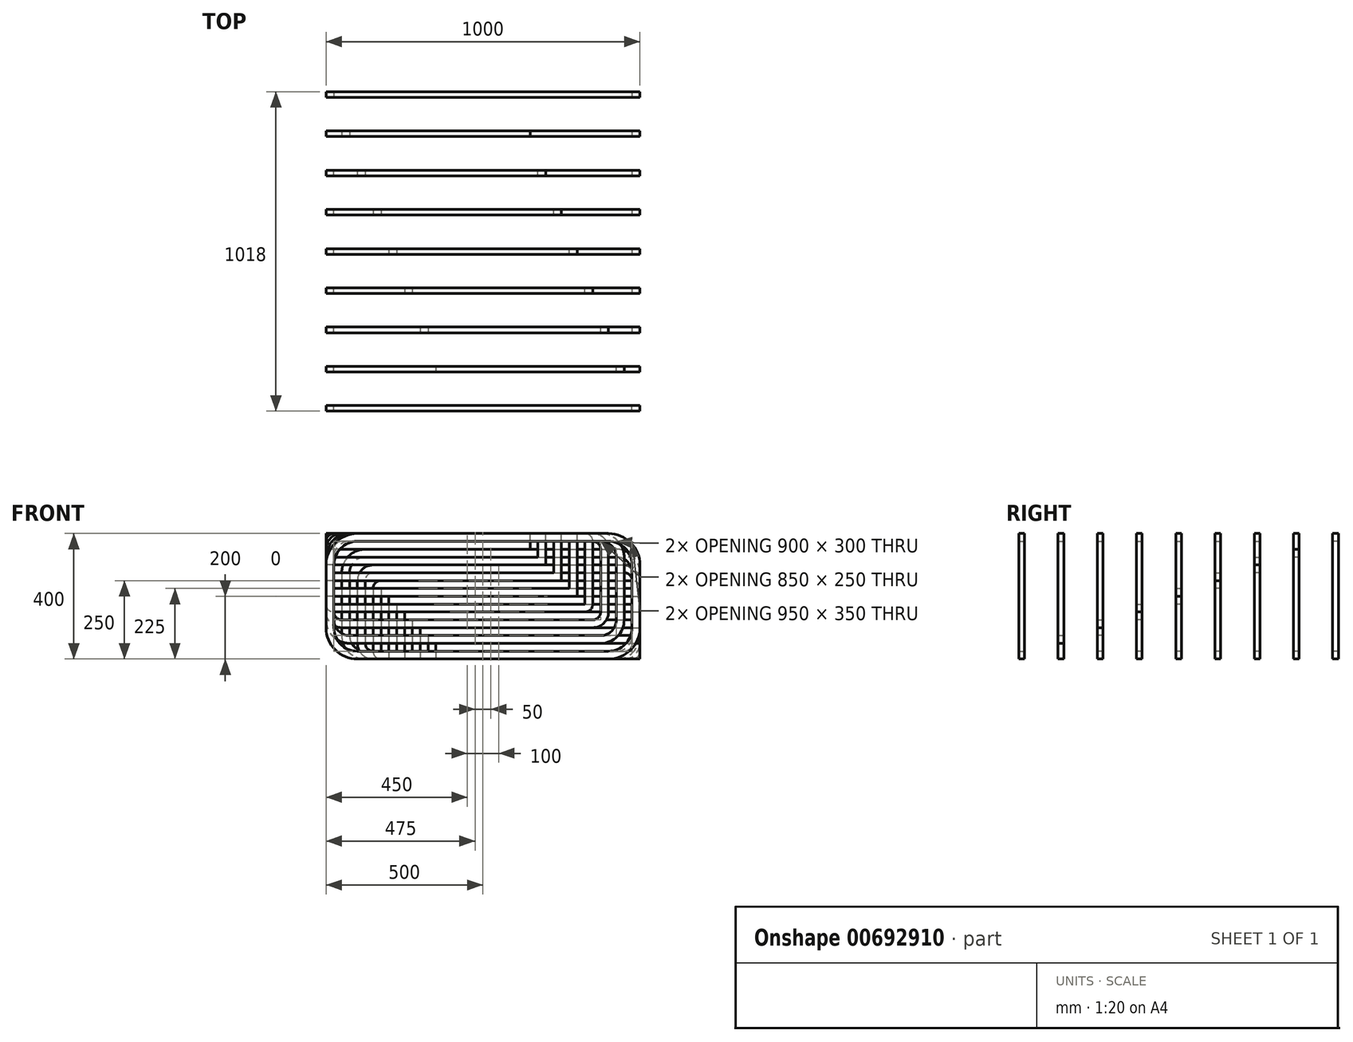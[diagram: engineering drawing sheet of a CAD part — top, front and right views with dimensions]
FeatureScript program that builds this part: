
annotation { "Feature Type Name" : "Feature", "Feature Type Description" : "" }
export const myFeature = defineFeature(function(context is Context, id is Id, definition is map)
    precondition{}
    {
        {
            assignVariable(context, id + "F0", {"name" : "thickness", "anyValue" : 18});
        }
        {
            assignVariable(context, id + "F1", {"name" : "length", "anyValue" : 1000});
        }
        {
            assignVariable(context, id + "F2", {"name" : "width", "anyValue" : getVariable(context, 'length')});
        }
        {
            assignVariable(context, id + "F3", {"name" : "stripwidth", "anyValue" : 25});
        }
        {
            assignVariable(context, id + "F4", {"name" : "interspace", "anyValue" : 5 * getVariable(context, 'stripwidth')});
        }
        {
            var Q0;
            Q0=qCreatedBy(makeId("Front.planeOp"),FACE);
            var sketch = newSketch(context, id + "F5", { "sketchPlane" : qUnion([Q0])});
            skLineSegment(sketch, "E0.bottom", {"start": v(-100, 0) * mm, "end": v(-900, 0) * mm});
            skLineSegment(sketch, "E0.top", {"start": v(-100, 400) * mm, "end": v(-900, 400) * mm});
            skLineSegment(sketch, "E0.left", {"start": v(0, 100) * mm, "end": v(0, 300) * mm});
            skLineSegment(sketch, "E0.right", {"start": v(-1000, 100) * mm, "end": v(-1000, 300) * mm});
            skPoint(sketch, "E1.visualSharp", {"position": v(-1000, 400) * mm});
            skArc(sketch, "E1.filletArc", {"start": v(-900, 400) * mm, "mid": v(-970.71, 370.71) * mm, "end": v(-1000, 300) * mm});
            skPoint(sketch, "E2.visualSharp", {"position": v(0, 400) * mm});
            skArc(sketch, "E2.filletArc", {"start": v(0, 300) * mm, "mid": v(-29.29, 370.71) * mm, "end": v(-100, 400) * mm});
            skPoint(sketch, "E3.visualSharp", {"position": v(0, 0) * mm});
            skArc(sketch, "E3.filletArc", {"start": v(-100, 0) * mm, "mid": v(-29.29, 29.29) * mm, "end": v(0, 100) * mm});
            skPoint(sketch, "E4.visualSharp", {"position": v(-1000, 0) * mm});
            skArc(sketch, "E4.filletArc", {"start": v(-1000, 100) * mm, "mid": v(-970.71, 29.29) * mm, "end": v(-900, 0) * mm});
            skLineSegment(sketch, "E5.0", {"start": v(-975, 100) * mm, "end": v(-975, 300) * mm});
            skArc(sketch, "E5.1", {"start": v(-900, 375) * mm, "mid": v(-953.03, 353.03) * mm, "end": v(-975, 300) * mm});
            skArc(sketch, "E5.2", {"start": v(-975, 100) * mm, "mid": v(-953.03, 46.97) * mm, "end": v(-900, 25) * mm});
            skLineSegment(sketch, "E5.3", {"start": v(-100, 375) * mm, "end": v(-900, 375) * mm});
            skLineSegment(sketch, "E5.4", {"start": v(-100, 25) * mm, "end": v(-900, 25) * mm});
            skArc(sketch, "E5.5", {"start": v(-100, 25) * mm, "mid": v(-46.97, 46.97) * mm, "end": v(-25, 100) * mm});
            skLineSegment(sketch, "E5.6", {"start": v(-25, 100) * mm, "end": v(-25, 300) * mm});
            skArc(sketch, "E5.7", {"start": v(-25, 300) * mm, "mid": v(-46.97, 353.03) * mm, "end": v(-100, 375) * mm});
            skArc(sketch, "E6.0", {"start": v(-50, 300) * mm, "mid": v(-64.64, 335.36) * mm, "end": v(-100, 350) * mm});
            skLineSegment(sketch, "E6.1", {"start": v(-50, 100) * mm, "end": v(-50, 300) * mm});
            skLineSegment(sketch, "E6.2", {"start": v(-100, 350) * mm, "end": v(-900, 350) * mm});
            skArc(sketch, "E6.3", {"start": v(-100, 50) * mm, "mid": v(-64.64, 64.64) * mm, "end": v(-50, 100) * mm});
            skArc(sketch, "E6.4", {"start": v(-900, 350) * mm, "mid": v(-935.36, 335.36) * mm, "end": v(-950, 300) * mm});
            skLineSegment(sketch, "E6.5", {"start": v(-950, 100) * mm, "end": v(-950, 300) * mm});
            skArc(sketch, "E6.6", {"start": v(-950, 100) * mm, "mid": v(-935.36, 64.64) * mm, "end": v(-900, 50) * mm});
            skLineSegment(sketch, "E6.7", {"start": v(-100, 50) * mm, "end": v(-900, 50) * mm});
            skLineSegment(sketch, "E7.0", {"start": v(-100, 325) * mm, "end": v(-900, 325) * mm});
            skArc(sketch, "E7.1", {"start": v(-75, 300) * mm, "mid": v(-82.32, 317.68) * mm, "end": v(-100, 325) * mm});
            skArc(sketch, "E7.2", {"start": v(-900, 325) * mm, "mid": v(-917.68, 317.68) * mm, "end": v(-925, 300) * mm});
            skLineSegment(sketch, "E7.3", {"start": v(-75, 100) * mm, "end": v(-75, 300) * mm});
            skLineSegment(sketch, "E7.4", {"start": v(-925, 100) * mm, "end": v(-925, 300) * mm});
            skArc(sketch, "E7.5", {"start": v(-925, 100) * mm, "mid": v(-917.68, 82.32) * mm, "end": v(-900, 75) * mm});
            skLineSegment(sketch, "E7.6", {"start": v(-100, 75) * mm, "end": v(-900, 75) * mm});
            skArc(sketch, "E7.7", {"start": v(-100, 75) * mm, "mid": v(-82.32, 82.32) * mm, "end": v(-75, 100) * mm});
            skLineSegment(sketch, "E8.0", {"start": v(-100, 300) * mm, "end": v(-900, 300) * mm});
            skLineSegment(sketch, "E8.1", {"start": v(-100, 300) * mm, "end": v(-100, 300) * mm});
            skLineSegment(sketch, "E8.2", {"start": v(-900, 300) * mm, "end": v(-900, 300) * mm});
            skLineSegment(sketch, "E8.3", {"start": v(-100, 100) * mm, "end": v(-100, 300) * mm});
            skLineSegment(sketch, "E8.4", {"start": v(-900, 100) * mm, "end": v(-900, 300) * mm});
            skLineSegment(sketch, "E8.5", {"start": v(-900, 100) * mm, "end": v(-900, 100) * mm});
            skLineSegment(sketch, "E8.6", {"start": v(-100, 100) * mm, "end": v(-900, 100) * mm});
            skLineSegment(sketch, "E8.7", {"start": v(-100, 100) * mm, "end": v(-100, 100) * mm});
            skLineSegment(sketch, "E9.0", {"start": v(-875, 125) * mm, "end": v(-875, 275) * mm});
            skLineSegment(sketch, "E9.1", {"start": v(-125, 125) * mm, "end": v(-875, 125) * mm});
            skLineSegment(sketch, "E9.2", {"start": v(-125, 125) * mm, "end": v(-125, 275) * mm});
            skLineSegment(sketch, "E9.3", {"start": v(-125, 275) * mm, "end": v(-875, 275) * mm});
            skLineSegment(sketch, "E10.0", {"start": v(-850, 150) * mm, "end": v(-850, 250) * mm});
            skLineSegment(sketch, "E10.1", {"start": v(-150, 150) * mm, "end": v(-850, 150) * mm});
            skLineSegment(sketch, "E10.2", {"start": v(-150, 150) * mm, "end": v(-150, 250) * mm});
            skLineSegment(sketch, "E10.3", {"start": v(-150, 250) * mm, "end": v(-850, 250) * mm});
            skLineSegment(sketch, "E11.0", {"start": v(-825, 175) * mm, "end": v(-825, 225) * mm});
            skLineSegment(sketch, "E11.1", {"start": v(-175, 175) * mm, "end": v(-825, 175) * mm});
            skLineSegment(sketch, "E11.2", {"start": v(-175, 175) * mm, "end": v(-175, 225) * mm});
            skLineSegment(sketch, "E11.3", {"start": v(-175, 225) * mm, "end": v(-825, 225) * mm});
            skSolve(sketch);
        }
        {
            var Q0;
            Q0=makeQuery(id+"F5.imprint","IMPRINT",FACE,{"disambiguationData":[TD([[makeQuery(id+"F5.imprint","IMPRINT",EDGE,{"derivedFrom":sQuery(id+"F5.wireOp",EDGE,"E0.bottom")}),-1.0]])]});
            extrude(context, id + "F6", {"entities" : qUnion([Q0]), "depth" : (getVariable(context, 'thickness')) * mm, "offsetDistance" : 25 * mm});
        }
        {
            var Q0;
            Q0=makeQuery(id+"F5.imprint","IMPRINT",FACE,{"disambiguationData":[TD([[makeQuery(id+"F5.imprint","IMPRINT",EDGE,{"derivedFrom":sQuery(id+"F5.wireOp",EDGE,"E5.0")}),-1.0]])]});
            extrude(context, id + "F7", {"entities" : qUnion([Q0]), "depth" : (getVariable(context, 'thickness')) * mm, "offsetDistance" : 25 * mm});
        }
        {
            var Q0;
            Q0=makeQuery(id+"F5.imprint","IMPRINT",FACE,{"disambiguationData":[TD([[makeQuery(id+"F5.imprint","IMPRINT",EDGE,{"derivedFrom":sQuery(id+"F5.wireOp",EDGE,"E6.0")}),1.0]])]});
            extrude(context, id + "F8", {"entities" : qUnion([Q0]), "depth" : (getVariable(context, 'thickness')) * mm, "offsetDistance" : 25 * mm});
        }
        {
            var Q0;
            Q0=makeQuery(id+"F5.imprint","IMPRINT",FACE,{"disambiguationData":[TD([[makeQuery(id+"F5.imprint","IMPRINT",EDGE,{"derivedFrom":sQuery(id+"F5.wireOp",EDGE,"E7.0")}),1.0]])]});
            extrude(context, id + "F9", {"entities" : qUnion([Q0]), "depth" : (getVariable(context, 'thickness')) * mm, "offsetDistance" : 25 * mm});
        }
        {
            var Q0;
            Q0=makeQuery(id+"F5.imprint","IMPRINT",FACE,{"disambiguationData":[TD([[makeQuery(id+"F5.imprint","IMPRINT",EDGE,{"derivedFrom":sQuery(id+"F5.wireOp",EDGE,"E8.0")}),1.0]])]});
            extrude(context, id + "F10", {"entities" : qUnion([Q0]), "depth" : (getVariable(context, 'thickness')) * mm, "offsetDistance" : 25 * mm});
        }
        {
            var Q0;
            Q0=makeQuery(id+"F5.imprint","IMPRINT",FACE,{"disambiguationData":[TD([[makeQuery(id+"F5.imprint","IMPRINT",EDGE,{"derivedFrom":sQuery(id+"F5.wireOp",EDGE,"E9.0")}),-1.0]])]});
            extrude(context, id + "F11", {"entities" : qUnion([Q0]), "depth" : (getVariable(context, 'thickness')) * mm, "offsetDistance" : 25 * mm});
        }
        {
            var Q0;
            Q0=makeQuery(id+"F5.imprint","IMPRINT",FACE,{"disambiguationData":[TD([[makeQuery(id+"F5.imprint","IMPRINT",EDGE,{"derivedFrom":sQuery(id+"F5.wireOp",EDGE,"E10.0")}),-1.0]])]});
            extrude(context, id + "F12", {"entities" : qUnion([Q0]), "depth" : (getVariable(context, 'thickness')) * mm, "offsetDistance" : 25 * mm});
        }
        {
            var Q0;
            Q0=makeQuery(id+"F5.imprint","IMPRINT",FACE,{"disambiguationData":[TD([[makeQuery(id+"F5.imprint","IMPRINT",EDGE,{"derivedFrom":sQuery(id+"F5.wireOp",EDGE,"E11.0")}),-1.0]])]});
            extrude(context, id + "F13", {"entities" : qUnion([Q0]), "depth" : (getVariable(context, 'thickness')) * mm, "offsetDistance" : 25 * mm});
        }
        {
            var Q0;
            Q0=makeQuery(id+"F7.opExtrude","SWEPT_BODY",BODY,{"disambiguationData":[OSD([sQuery(id+"F5.wireOp",EDGE,"E5.0"),sQuery(id+"F5.wireOp",EDGE,"E5.1"),sQuery(id+"F5.wireOp",EDGE,"E5.2"),sQuery(id+"F5.wireOp",EDGE,"E5.3"),sQuery(id+"F5.wireOp",EDGE,"E5.4"),sQuery(id+"F5.wireOp",EDGE,"E5.5"),sQuery(id+"F5.wireOp",EDGE,"E5.6"),sQuery(id+"F5.wireOp",EDGE,"E5.7"),sQuery(id+"F5.wireOp",EDGE,"E6.0"),sQuery(id+"F5.wireOp",EDGE,"E6.1"),sQuery(id+"F5.wireOp",EDGE,"E6.2"),sQuery(id+"F5.wireOp",EDGE,"E6.3"),sQuery(id+"F5.wireOp",EDGE,"E6.4"),sQuery(id+"F5.wireOp",EDGE,"E6.5"),sQuery(id+"F5.wireOp",EDGE,"E6.6"),sQuery(id+"F5.wireOp",EDGE,"E6.7")])]});
            transform(context, id + "F14", {"entities" : qUnion([Q0]), "transformType" : TransformType.TRANSLATION_3D, "dx" : (-getVariable(context, 'stripwidth')) * mm, "dy" : (getVariable(context, 'interspace')) * mm, "dz" : (getVariable(context, 'stripwidth')) * mm, "makeCopy" : false});
        }
        {
            var Q0;
            Q0=makeQuery(id+"F8.opExtrude","SWEPT_BODY",BODY,{"disambiguationData":[OSD([sQuery(id+"F5.wireOp",EDGE,"E6.0"),sQuery(id+"F5.wireOp",EDGE,"E6.1"),sQuery(id+"F5.wireOp",EDGE,"E6.2"),sQuery(id+"F5.wireOp",EDGE,"E6.3"),sQuery(id+"F5.wireOp",EDGE,"E6.4"),sQuery(id+"F5.wireOp",EDGE,"E6.5"),sQuery(id+"F5.wireOp",EDGE,"E6.6"),sQuery(id+"F5.wireOp",EDGE,"E6.7"),sQuery(id+"F5.wireOp",EDGE,"E7.0"),sQuery(id+"F5.wireOp",EDGE,"E7.1"),sQuery(id+"F5.wireOp",EDGE,"E7.2"),sQuery(id+"F5.wireOp",EDGE,"E7.3"),sQuery(id+"F5.wireOp",EDGE,"E7.4"),sQuery(id+"F5.wireOp",EDGE,"E7.5"),sQuery(id+"F5.wireOp",EDGE,"E7.6"),sQuery(id+"F5.wireOp",EDGE,"E7.7")])]});
            transform(context, id + "F15", {"entities" : qUnion([Q0]), "transformType" : TransformType.TRANSLATION_3D, "dx" : (-2 * getVariable(context, 'stripwidth')) * mm, "dy" : (2 * getVariable(context, 'interspace')) * mm, "dz" : (2 * getVariable(context, 'stripwidth')) * mm, "makeCopy" : false});
        }
        {
            var Q0;
            Q0=makeQuery(id+"F9.opExtrude","SWEPT_BODY",BODY,{"disambiguationData":[OSD([sQuery(id+"F5.wireOp",EDGE,"E7.0"),sQuery(id+"F5.wireOp",EDGE,"E7.1"),sQuery(id+"F5.wireOp",EDGE,"E7.2"),sQuery(id+"F5.wireOp",EDGE,"E7.3"),sQuery(id+"F5.wireOp",EDGE,"E7.4"),sQuery(id+"F5.wireOp",EDGE,"E7.5"),sQuery(id+"F5.wireOp",EDGE,"E7.6"),sQuery(id+"F5.wireOp",EDGE,"E7.7"),sQuery(id+"F5.wireOp",EDGE,"E8.0"),sQuery(id+"F5.wireOp",EDGE,"E8.3"),sQuery(id+"F5.wireOp",EDGE,"E8.4"),sQuery(id+"F5.wireOp",EDGE,"E8.6")])]});
            transform(context, id + "F16", {"entities" : qUnion([Q0]), "transformType" : TransformType.TRANSLATION_3D, "dx" : (-3 * getVariable(context, 'stripwidth')) * mm, "dy" : (3 * getVariable(context, 'interspace')) * mm, "dz" : (3 * getVariable(context, 'stripwidth')) * mm, "makeCopy" : false});
        }
        {
            var Q0;
            Q0=makeQuery(id+"F10.opExtrude","SWEPT_BODY",BODY,{"disambiguationData":[OSD([sQuery(id+"F5.wireOp",EDGE,"E8.0"),sQuery(id+"F5.wireOp",EDGE,"E8.3"),sQuery(id+"F5.wireOp",EDGE,"E8.4"),sQuery(id+"F5.wireOp",EDGE,"E8.6"),sQuery(id+"F5.wireOp",EDGE,"E9.0"),sQuery(id+"F5.wireOp",EDGE,"E9.1"),sQuery(id+"F5.wireOp",EDGE,"E9.2"),sQuery(id+"F5.wireOp",EDGE,"E9.3")])]});
            transform(context, id + "F17", {"entities" : qUnion([Q0]), "transformType" : TransformType.TRANSLATION_3D, "dx" : (-4 * getVariable(context, 'stripwidth')) * mm, "dy" : (4 * getVariable(context, 'interspace')) * mm, "dz" : (4 * getVariable(context, 'stripwidth')) * mm, "makeCopy" : false});
        }
        {
            var Q0;
            Q0=makeQuery(id+"F11.opExtrude","SWEPT_BODY",BODY,{"disambiguationData":[OSD([sQuery(id+"F5.wireOp",EDGE,"E9.0"),sQuery(id+"F5.wireOp",EDGE,"E9.1"),sQuery(id+"F5.wireOp",EDGE,"E9.2"),sQuery(id+"F5.wireOp",EDGE,"E9.3"),sQuery(id+"F5.wireOp",EDGE,"E10.0"),sQuery(id+"F5.wireOp",EDGE,"E10.1"),sQuery(id+"F5.wireOp",EDGE,"E10.2"),sQuery(id+"F5.wireOp",EDGE,"E10.3")])]});
            transform(context, id + "F18", {"entities" : qUnion([Q0]), "transformType" : TransformType.TRANSLATION_3D, "dx" : (-5 * getVariable(context, 'stripwidth')) * mm, "dy" : (5 * getVariable(context, 'interspace')) * mm, "dz" : (5 * getVariable(context, 'stripwidth')) * mm, "makeCopy" : false});
        }
        {
            var Q0;
            Q0=makeQuery(id+"F12.opExtrude","SWEPT_BODY",BODY,{"disambiguationData":[OSD([sQuery(id+"F5.wireOp",EDGE,"E10.0"),sQuery(id+"F5.wireOp",EDGE,"E10.1"),sQuery(id+"F5.wireOp",EDGE,"E10.2"),sQuery(id+"F5.wireOp",EDGE,"E10.3"),sQuery(id+"F5.wireOp",EDGE,"E11.0"),sQuery(id+"F5.wireOp",EDGE,"E11.1"),sQuery(id+"F5.wireOp",EDGE,"E11.2"),sQuery(id+"F5.wireOp",EDGE,"E11.3")])]});
            transform(context, id + "F19", {"entities" : qUnion([Q0]), "transformType" : TransformType.TRANSLATION_3D, "dx" : (-6 * getVariable(context, 'stripwidth')) * mm, "dy" : (6 * getVariable(context, 'interspace')) * mm, "dz" : (6 * getVariable(context, 'stripwidth')) * mm, "makeCopy" : false});
        }
        {
            var Q0;
            Q0=makeQuery(id+"F13.opExtrude","SWEPT_BODY",BODY,{"disambiguationData":[OSD([sQuery(id+"F5.wireOp",EDGE,"E11.0"),sQuery(id+"F5.wireOp",EDGE,"E11.1"),sQuery(id+"F5.wireOp",EDGE,"E11.2"),sQuery(id+"F5.wireOp",EDGE,"E11.3")])]});
            transform(context, id + "F20", {"entities" : qUnion([Q0]), "transformType" : TransformType.TRANSLATION_3D, "dx" : (-7 * getVariable(context, 'stripwidth')) * mm, "dy" : (7 * getVariable(context, 'interspace')) * mm, "dz" : (7 * getVariable(context, 'stripwidth')) * mm, "makeCopy" : false});
        }
        {
            var Q0;
            Q0=makeQuery(id+"F6.opExtrude","SWEPT_BODY",BODY,{"disambiguationData":[OSD([sQuery(id+"F5.wireOp",EDGE,"E0.bottom"),sQuery(id+"F5.wireOp",EDGE,"E0.top"),sQuery(id+"F5.wireOp",EDGE,"E0.left"),sQuery(id+"F5.wireOp",EDGE,"E0.right"),sQuery(id+"F5.wireOp",EDGE,"E1.filletArc"),sQuery(id+"F5.wireOp",EDGE,"E2.filletArc"),sQuery(id+"F5.wireOp",EDGE,"E3.filletArc"),sQuery(id+"F5.wireOp",EDGE,"E4.filletArc"),sQuery(id+"F5.wireOp",EDGE,"E5.0"),sQuery(id+"F5.wireOp",EDGE,"E5.1"),sQuery(id+"F5.wireOp",EDGE,"E5.2"),sQuery(id+"F5.wireOp",EDGE,"E5.3"),sQuery(id+"F5.wireOp",EDGE,"E5.4"),sQuery(id+"F5.wireOp",EDGE,"E5.5"),sQuery(id+"F5.wireOp",EDGE,"E5.6"),sQuery(id+"F5.wireOp",EDGE,"E5.7")])]});
            var Q1;
            Q1=makeQuery(id+"F8.opExtrude","SWEPT_BODY",BODY,{"disambiguationData":[OSD([sQuery(id+"F5.wireOp",EDGE,"E6.0"),sQuery(id+"F5.wireOp",EDGE,"E6.1"),sQuery(id+"F5.wireOp",EDGE,"E6.2"),sQuery(id+"F5.wireOp",EDGE,"E6.3"),sQuery(id+"F5.wireOp",EDGE,"E6.4"),sQuery(id+"F5.wireOp",EDGE,"E6.5"),sQuery(id+"F5.wireOp",EDGE,"E6.6"),sQuery(id+"F5.wireOp",EDGE,"E6.7"),sQuery(id+"F5.wireOp",EDGE,"E7.0"),sQuery(id+"F5.wireOp",EDGE,"E7.1"),sQuery(id+"F5.wireOp",EDGE,"E7.2"),sQuery(id+"F5.wireOp",EDGE,"E7.3"),sQuery(id+"F5.wireOp",EDGE,"E7.4"),sQuery(id+"F5.wireOp",EDGE,"E7.5"),sQuery(id+"F5.wireOp",EDGE,"E7.6"),sQuery(id+"F5.wireOp",EDGE,"E7.7")])]});
            var Q2;
            Q2=makeQuery(id+"F7.opExtrude","SWEPT_BODY",BODY,{"disambiguationData":[OSD([sQuery(id+"F5.wireOp",EDGE,"E5.0"),sQuery(id+"F5.wireOp",EDGE,"E5.1"),sQuery(id+"F5.wireOp",EDGE,"E5.2"),sQuery(id+"F5.wireOp",EDGE,"E5.3"),sQuery(id+"F5.wireOp",EDGE,"E5.4"),sQuery(id+"F5.wireOp",EDGE,"E5.5"),sQuery(id+"F5.wireOp",EDGE,"E5.6"),sQuery(id+"F5.wireOp",EDGE,"E5.7"),sQuery(id+"F5.wireOp",EDGE,"E6.0"),sQuery(id+"F5.wireOp",EDGE,"E6.1"),sQuery(id+"F5.wireOp",EDGE,"E6.2"),sQuery(id+"F5.wireOp",EDGE,"E6.3"),sQuery(id+"F5.wireOp",EDGE,"E6.4"),sQuery(id+"F5.wireOp",EDGE,"E6.5"),sQuery(id+"F5.wireOp",EDGE,"E6.6"),sQuery(id+"F5.wireOp",EDGE,"E6.7")])]});
            var Q3;
            Q3=makeQuery(id+"F13.opExtrude","SWEPT_BODY",BODY,{"disambiguationData":[OSD([sQuery(id+"F5.wireOp",EDGE,"E11.0"),sQuery(id+"F5.wireOp",EDGE,"E11.1"),sQuery(id+"F5.wireOp",EDGE,"E11.2"),sQuery(id+"F5.wireOp",EDGE,"E11.3")])]});
            var Q4;
            Q4=makeQuery(id+"F12.opExtrude","SWEPT_BODY",BODY,{"disambiguationData":[OSD([sQuery(id+"F5.wireOp",EDGE,"E10.0"),sQuery(id+"F5.wireOp",EDGE,"E10.1"),sQuery(id+"F5.wireOp",EDGE,"E10.2"),sQuery(id+"F5.wireOp",EDGE,"E10.3"),sQuery(id+"F5.wireOp",EDGE,"E11.0"),sQuery(id+"F5.wireOp",EDGE,"E11.1"),sQuery(id+"F5.wireOp",EDGE,"E11.2"),sQuery(id+"F5.wireOp",EDGE,"E11.3")])]});
            var Q5;
            Q5=makeQuery(id+"F11.opExtrude","SWEPT_BODY",BODY,{"disambiguationData":[OSD([sQuery(id+"F5.wireOp",EDGE,"E9.0"),sQuery(id+"F5.wireOp",EDGE,"E9.1"),sQuery(id+"F5.wireOp",EDGE,"E9.2"),sQuery(id+"F5.wireOp",EDGE,"E9.3"),sQuery(id+"F5.wireOp",EDGE,"E10.0"),sQuery(id+"F5.wireOp",EDGE,"E10.1"),sQuery(id+"F5.wireOp",EDGE,"E10.2"),sQuery(id+"F5.wireOp",EDGE,"E10.3")])]});
            var Q6;
            Q6=makeQuery(id+"F9.opExtrude","SWEPT_BODY",BODY,{"disambiguationData":[OSD([sQuery(id+"F5.wireOp",EDGE,"E7.0"),sQuery(id+"F5.wireOp",EDGE,"E7.1"),sQuery(id+"F5.wireOp",EDGE,"E7.2"),sQuery(id+"F5.wireOp",EDGE,"E7.3"),sQuery(id+"F5.wireOp",EDGE,"E7.4"),sQuery(id+"F5.wireOp",EDGE,"E7.5"),sQuery(id+"F5.wireOp",EDGE,"E7.6"),sQuery(id+"F5.wireOp",EDGE,"E7.7"),sQuery(id+"F5.wireOp",EDGE,"E8.0"),sQuery(id+"F5.wireOp",EDGE,"E8.3"),sQuery(id+"F5.wireOp",EDGE,"E8.4"),sQuery(id+"F5.wireOp",EDGE,"E8.6")])]});
            var Q7;
            Q7=makeQuery(id+"F10.opExtrude","SWEPT_BODY",BODY,{"disambiguationData":[OSD([sQuery(id+"F5.wireOp",EDGE,"E8.0"),sQuery(id+"F5.wireOp",EDGE,"E8.3"),sQuery(id+"F5.wireOp",EDGE,"E8.4"),sQuery(id+"F5.wireOp",EDGE,"E8.6"),sQuery(id+"F5.wireOp",EDGE,"E9.0"),sQuery(id+"F5.wireOp",EDGE,"E9.1"),sQuery(id+"F5.wireOp",EDGE,"E9.2"),sQuery(id+"F5.wireOp",EDGE,"E9.3")])]});
            var Q8;
            Q8=qCreatedBy(makeId("Right.planeOp"),FACE);
            mirror(context, id + "F21", {"entities" : qUnion([Q0, Q1, Q2, Q3, Q4, Q5, Q6, Q7]), "mirrorPlane" : qUnion([Q8])});
        }
        {
            var Q0;
            Q0=makeQuery(id+"F21.opPattern","COPY",BODY,{"derivedFrom":makeQuery(id+"F8.opExtrude","SWEPT_BODY",BODY,{"disambiguationData":[OSD([sQuery(id+"F5.wireOp",EDGE,"E6.0"),sQuery(id+"F5.wireOp",EDGE,"E6.1"),sQuery(id+"F5.wireOp",EDGE,"E6.2"),sQuery(id+"F5.wireOp",EDGE,"E6.3"),sQuery(id+"F5.wireOp",EDGE,"E6.4"),sQuery(id+"F5.wireOp",EDGE,"E6.5"),sQuery(id+"F5.wireOp",EDGE,"E6.6"),sQuery(id+"F5.wireOp",EDGE,"E6.7"),sQuery(id+"F5.wireOp",EDGE,"E7.0"),sQuery(id+"F5.wireOp",EDGE,"E7.1"),sQuery(id+"F5.wireOp",EDGE,"E7.2"),sQuery(id+"F5.wireOp",EDGE,"E7.3"),sQuery(id+"F5.wireOp",EDGE,"E7.4"),sQuery(id+"F5.wireOp",EDGE,"E7.5"),sQuery(id+"F5.wireOp",EDGE,"E7.6"),sQuery(id+"F5.wireOp",EDGE,"E7.7")])]}),"instanceName":"1"});
            var Q1;
            Q1=makeQuery(id+"F21.opPattern","COPY",BODY,{"derivedFrom":makeQuery(id+"F9.opExtrude","SWEPT_BODY",BODY,{"disambiguationData":[OSD([sQuery(id+"F5.wireOp",EDGE,"E7.0"),sQuery(id+"F5.wireOp",EDGE,"E7.1"),sQuery(id+"F5.wireOp",EDGE,"E7.2"),sQuery(id+"F5.wireOp",EDGE,"E7.3"),sQuery(id+"F5.wireOp",EDGE,"E7.4"),sQuery(id+"F5.wireOp",EDGE,"E7.5"),sQuery(id+"F5.wireOp",EDGE,"E7.6"),sQuery(id+"F5.wireOp",EDGE,"E7.7"),sQuery(id+"F5.wireOp",EDGE,"E8.0"),sQuery(id+"F5.wireOp",EDGE,"E8.3"),sQuery(id+"F5.wireOp",EDGE,"E8.4"),sQuery(id+"F5.wireOp",EDGE,"E8.6")])]}),"instanceName":"1"});
            var Q2;
            Q2=makeQuery(id+"F21.opPattern","COPY",BODY,{"derivedFrom":makeQuery(id+"F12.opExtrude","SWEPT_BODY",BODY,{"disambiguationData":[OSD([sQuery(id+"F5.wireOp",EDGE,"E10.0"),sQuery(id+"F5.wireOp",EDGE,"E10.1"),sQuery(id+"F5.wireOp",EDGE,"E10.2"),sQuery(id+"F5.wireOp",EDGE,"E10.3"),sQuery(id+"F5.wireOp",EDGE,"E11.0"),sQuery(id+"F5.wireOp",EDGE,"E11.1"),sQuery(id+"F5.wireOp",EDGE,"E11.2"),sQuery(id+"F5.wireOp",EDGE,"E11.3")])]}),"instanceName":"1"});
            var Q3;
            Q3=makeQuery(id+"F21.opPattern","COPY",BODY,{"derivedFrom":makeQuery(id+"F7.opExtrude","SWEPT_BODY",BODY,{"disambiguationData":[OSD([sQuery(id+"F5.wireOp",EDGE,"E5.0"),sQuery(id+"F5.wireOp",EDGE,"E5.1"),sQuery(id+"F5.wireOp",EDGE,"E5.2"),sQuery(id+"F5.wireOp",EDGE,"E5.3"),sQuery(id+"F5.wireOp",EDGE,"E5.4"),sQuery(id+"F5.wireOp",EDGE,"E5.5"),sQuery(id+"F5.wireOp",EDGE,"E5.6"),sQuery(id+"F5.wireOp",EDGE,"E5.7"),sQuery(id+"F5.wireOp",EDGE,"E6.0"),sQuery(id+"F5.wireOp",EDGE,"E6.1"),sQuery(id+"F5.wireOp",EDGE,"E6.2"),sQuery(id+"F5.wireOp",EDGE,"E6.3"),sQuery(id+"F5.wireOp",EDGE,"E6.4"),sQuery(id+"F5.wireOp",EDGE,"E6.5"),sQuery(id+"F5.wireOp",EDGE,"E6.6"),sQuery(id+"F5.wireOp",EDGE,"E6.7")])]}),"instanceName":"1"});
            var Q4;
            Q4=makeQuery(id+"F21.opPattern","COPY",BODY,{"derivedFrom":makeQuery(id+"F10.opExtrude","SWEPT_BODY",BODY,{"disambiguationData":[OSD([sQuery(id+"F5.wireOp",EDGE,"E8.0"),sQuery(id+"F5.wireOp",EDGE,"E8.3"),sQuery(id+"F5.wireOp",EDGE,"E8.4"),sQuery(id+"F5.wireOp",EDGE,"E8.6"),sQuery(id+"F5.wireOp",EDGE,"E9.0"),sQuery(id+"F5.wireOp",EDGE,"E9.1"),sQuery(id+"F5.wireOp",EDGE,"E9.2"),sQuery(id+"F5.wireOp",EDGE,"E9.3")])]}),"instanceName":"1"});
            var Q5;
            Q5=makeQuery(id+"F21.opPattern","COPY",BODY,{"derivedFrom":makeQuery(id+"F13.opExtrude","SWEPT_BODY",BODY,{"disambiguationData":[OSD([sQuery(id+"F5.wireOp",EDGE,"E11.0"),sQuery(id+"F5.wireOp",EDGE,"E11.1"),sQuery(id+"F5.wireOp",EDGE,"E11.2"),sQuery(id+"F5.wireOp",EDGE,"E11.3")])]}),"instanceName":"1"});
            var Q6;
            Q6=makeQuery(id+"F21.opPattern","COPY",BODY,{"derivedFrom":makeQuery(id+"F11.opExtrude","SWEPT_BODY",BODY,{"disambiguationData":[OSD([sQuery(id+"F5.wireOp",EDGE,"E9.0"),sQuery(id+"F5.wireOp",EDGE,"E9.1"),sQuery(id+"F5.wireOp",EDGE,"E9.2"),sQuery(id+"F5.wireOp",EDGE,"E9.3"),sQuery(id+"F5.wireOp",EDGE,"E10.0"),sQuery(id+"F5.wireOp",EDGE,"E10.1"),sQuery(id+"F5.wireOp",EDGE,"E10.2"),sQuery(id+"F5.wireOp",EDGE,"E10.3")])]}),"instanceName":"1"});
            var Q7;
            Q7=makeQuery(id+"F21.opPattern","COPY",BODY,{"derivedFrom":makeQuery(id+"F6.opExtrude","SWEPT_BODY",BODY,{"disambiguationData":[OSD([sQuery(id+"F5.wireOp",EDGE,"E0.bottom"),sQuery(id+"F5.wireOp",EDGE,"E0.top"),sQuery(id+"F5.wireOp",EDGE,"E0.left"),sQuery(id+"F5.wireOp",EDGE,"E0.right"),sQuery(id+"F5.wireOp",EDGE,"E1.filletArc"),sQuery(id+"F5.wireOp",EDGE,"E2.filletArc"),sQuery(id+"F5.wireOp",EDGE,"E3.filletArc"),sQuery(id+"F5.wireOp",EDGE,"E4.filletArc"),sQuery(id+"F5.wireOp",EDGE,"E5.0"),sQuery(id+"F5.wireOp",EDGE,"E5.1"),sQuery(id+"F5.wireOp",EDGE,"E5.2"),sQuery(id+"F5.wireOp",EDGE,"E5.3"),sQuery(id+"F5.wireOp",EDGE,"E5.4"),sQuery(id+"F5.wireOp",EDGE,"E5.5"),sQuery(id+"F5.wireOp",EDGE,"E5.6"),sQuery(id+"F5.wireOp",EDGE,"E5.7")])]}),"instanceName":"1"});
            var Q8;
            Q8=makeQuery(id+"F21.opPattern","COPY",EDGE,{"derivedFrom":makeQuery(id+"F6.opExtrude","CAP_EDGE",EDGE,{"disambiguationData":[OSD([sQuery(id+"F5.wireOp",EDGE,"E0.bottom")])],"isStart":false}),"instanceName":"1"});
            transform(context, id + "F22", {"entities" : qUnion([Q0, Q1, Q2, Q3, Q4, Q5, Q6, Q7]), "transformType" : TransformType.ROTATION, "transformAxis" : qUnion([Q8]), "angle" : 180 * degree, "makeCopy" : false});
        }
        {
            var Q0;
            Q0=makeQuery(id+"F21.opPattern","COPY",BODY,{"derivedFrom":makeQuery(id+"F10.opExtrude","SWEPT_BODY",BODY,{"disambiguationData":[OSD([sQuery(id+"F5.wireOp",EDGE,"E8.0"),sQuery(id+"F5.wireOp",EDGE,"E8.3"),sQuery(id+"F5.wireOp",EDGE,"E8.4"),sQuery(id+"F5.wireOp",EDGE,"E8.6"),sQuery(id+"F5.wireOp",EDGE,"E9.0"),sQuery(id+"F5.wireOp",EDGE,"E9.1"),sQuery(id+"F5.wireOp",EDGE,"E9.2"),sQuery(id+"F5.wireOp",EDGE,"E9.3")])]}),"instanceName":"1"});
            var Q1;
            Q1=makeQuery(id+"F21.opPattern","COPY",BODY,{"derivedFrom":makeQuery(id+"F9.opExtrude","SWEPT_BODY",BODY,{"disambiguationData":[OSD([sQuery(id+"F5.wireOp",EDGE,"E7.0"),sQuery(id+"F5.wireOp",EDGE,"E7.1"),sQuery(id+"F5.wireOp",EDGE,"E7.2"),sQuery(id+"F5.wireOp",EDGE,"E7.3"),sQuery(id+"F5.wireOp",EDGE,"E7.4"),sQuery(id+"F5.wireOp",EDGE,"E7.5"),sQuery(id+"F5.wireOp",EDGE,"E7.6"),sQuery(id+"F5.wireOp",EDGE,"E7.7"),sQuery(id+"F5.wireOp",EDGE,"E8.0"),sQuery(id+"F5.wireOp",EDGE,"E8.3"),sQuery(id+"F5.wireOp",EDGE,"E8.4"),sQuery(id+"F5.wireOp",EDGE,"E8.6")])]}),"instanceName":"1"});
            var Q2;
            Q2=makeQuery(id+"F21.opPattern","COPY",BODY,{"derivedFrom":makeQuery(id+"F13.opExtrude","SWEPT_BODY",BODY,{"disambiguationData":[OSD([sQuery(id+"F5.wireOp",EDGE,"E11.0"),sQuery(id+"F5.wireOp",EDGE,"E11.1"),sQuery(id+"F5.wireOp",EDGE,"E11.2"),sQuery(id+"F5.wireOp",EDGE,"E11.3")])]}),"instanceName":"1"});
            var Q3;
            Q3=makeQuery(id+"F21.opPattern","COPY",BODY,{"derivedFrom":makeQuery(id+"F11.opExtrude","SWEPT_BODY",BODY,{"disambiguationData":[OSD([sQuery(id+"F5.wireOp",EDGE,"E9.0"),sQuery(id+"F5.wireOp",EDGE,"E9.1"),sQuery(id+"F5.wireOp",EDGE,"E9.2"),sQuery(id+"F5.wireOp",EDGE,"E9.3"),sQuery(id+"F5.wireOp",EDGE,"E10.0"),sQuery(id+"F5.wireOp",EDGE,"E10.1"),sQuery(id+"F5.wireOp",EDGE,"E10.2"),sQuery(id+"F5.wireOp",EDGE,"E10.3")])]}),"instanceName":"1"});
            var Q4;
            Q4=makeQuery(id+"F21.opPattern","COPY",BODY,{"derivedFrom":makeQuery(id+"F8.opExtrude","SWEPT_BODY",BODY,{"disambiguationData":[OSD([sQuery(id+"F5.wireOp",EDGE,"E6.0"),sQuery(id+"F5.wireOp",EDGE,"E6.1"),sQuery(id+"F5.wireOp",EDGE,"E6.2"),sQuery(id+"F5.wireOp",EDGE,"E6.3"),sQuery(id+"F5.wireOp",EDGE,"E6.4"),sQuery(id+"F5.wireOp",EDGE,"E6.5"),sQuery(id+"F5.wireOp",EDGE,"E6.6"),sQuery(id+"F5.wireOp",EDGE,"E6.7"),sQuery(id+"F5.wireOp",EDGE,"E7.0"),sQuery(id+"F5.wireOp",EDGE,"E7.1"),sQuery(id+"F5.wireOp",EDGE,"E7.2"),sQuery(id+"F5.wireOp",EDGE,"E7.3"),sQuery(id+"F5.wireOp",EDGE,"E7.4"),sQuery(id+"F5.wireOp",EDGE,"E7.5"),sQuery(id+"F5.wireOp",EDGE,"E7.6"),sQuery(id+"F5.wireOp",EDGE,"E7.7")])]}),"instanceName":"1"});
            var Q5;
            Q5=makeQuery(id+"F21.opPattern","COPY",BODY,{"derivedFrom":makeQuery(id+"F7.opExtrude","SWEPT_BODY",BODY,{"disambiguationData":[OSD([sQuery(id+"F5.wireOp",EDGE,"E5.0"),sQuery(id+"F5.wireOp",EDGE,"E5.1"),sQuery(id+"F5.wireOp",EDGE,"E5.2"),sQuery(id+"F5.wireOp",EDGE,"E5.3"),sQuery(id+"F5.wireOp",EDGE,"E5.4"),sQuery(id+"F5.wireOp",EDGE,"E5.5"),sQuery(id+"F5.wireOp",EDGE,"E5.6"),sQuery(id+"F5.wireOp",EDGE,"E5.7"),sQuery(id+"F5.wireOp",EDGE,"E6.0"),sQuery(id+"F5.wireOp",EDGE,"E6.1"),sQuery(id+"F5.wireOp",EDGE,"E6.2"),sQuery(id+"F5.wireOp",EDGE,"E6.3"),sQuery(id+"F5.wireOp",EDGE,"E6.4"),sQuery(id+"F5.wireOp",EDGE,"E6.5"),sQuery(id+"F5.wireOp",EDGE,"E6.6"),sQuery(id+"F5.wireOp",EDGE,"E6.7")])]}),"instanceName":"1"});
            var Q6;
            Q6=makeQuery(id+"F21.opPattern","COPY",BODY,{"derivedFrom":makeQuery(id+"F12.opExtrude","SWEPT_BODY",BODY,{"disambiguationData":[OSD([sQuery(id+"F5.wireOp",EDGE,"E10.0"),sQuery(id+"F5.wireOp",EDGE,"E10.1"),sQuery(id+"F5.wireOp",EDGE,"E10.2"),sQuery(id+"F5.wireOp",EDGE,"E10.3"),sQuery(id+"F5.wireOp",EDGE,"E11.0"),sQuery(id+"F5.wireOp",EDGE,"E11.1"),sQuery(id+"F5.wireOp",EDGE,"E11.2"),sQuery(id+"F5.wireOp",EDGE,"E11.3")])]}),"instanceName":"1"});
            var Q7;
            Q7=makeQuery(id+"F21.opPattern","COPY",BODY,{"derivedFrom":makeQuery(id+"F6.opExtrude","SWEPT_BODY",BODY,{"disambiguationData":[OSD([sQuery(id+"F5.wireOp",EDGE,"E0.bottom"),sQuery(id+"F5.wireOp",EDGE,"E0.top"),sQuery(id+"F5.wireOp",EDGE,"E0.left"),sQuery(id+"F5.wireOp",EDGE,"E0.right"),sQuery(id+"F5.wireOp",EDGE,"E1.filletArc"),sQuery(id+"F5.wireOp",EDGE,"E2.filletArc"),sQuery(id+"F5.wireOp",EDGE,"E3.filletArc"),sQuery(id+"F5.wireOp",EDGE,"E4.filletArc"),sQuery(id+"F5.wireOp",EDGE,"E5.0"),sQuery(id+"F5.wireOp",EDGE,"E5.1"),sQuery(id+"F5.wireOp",EDGE,"E5.2"),sQuery(id+"F5.wireOp",EDGE,"E5.3"),sQuery(id+"F5.wireOp",EDGE,"E5.4"),sQuery(id+"F5.wireOp",EDGE,"E5.5"),sQuery(id+"F5.wireOp",EDGE,"E5.6"),sQuery(id+"F5.wireOp",EDGE,"E5.7")])]}),"instanceName":"1"});
            transform(context, id + "F23", {"entities" : qUnion([Q0, Q1, Q2, Q3, Q4, Q5, Q6, Q7]), "transformType" : TransformType.TRANSLATION_3D, "dx" : (-getVariable(context, 'width')) * mm, "dy" : ((8 * getVariable(context, 'interspace')) + getVariable(context, 'thickness')) * mm, "dz" : (16 * getVariable(context, 'stripwidth')) * mm, "makeCopy" : false});
        }
    });
